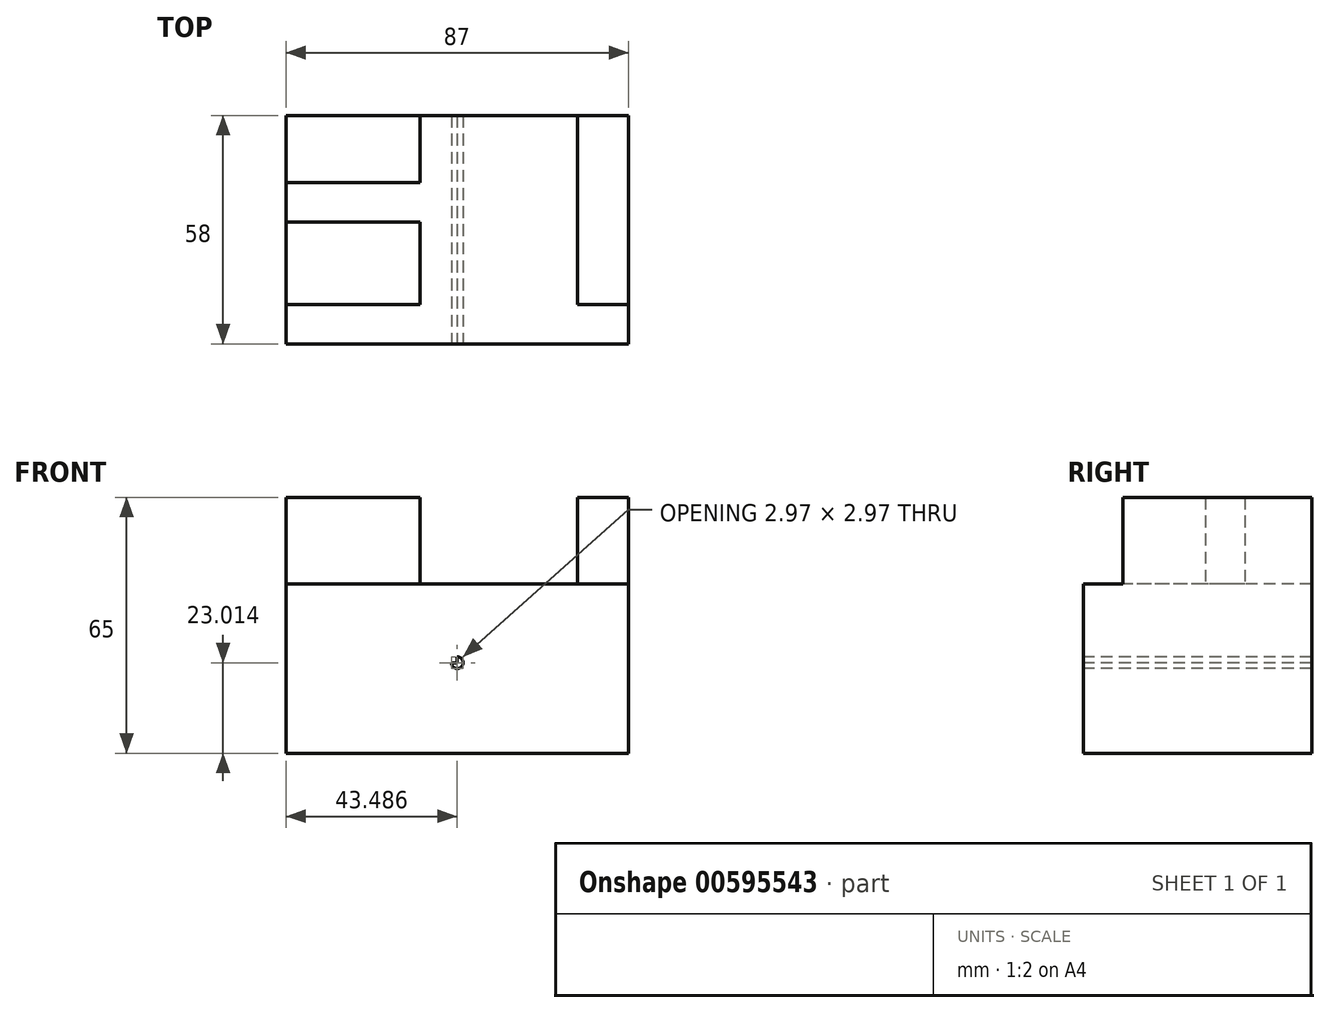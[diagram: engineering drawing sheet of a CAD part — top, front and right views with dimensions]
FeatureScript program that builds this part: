
annotation { "Feature Type Name" : "Feature", "Feature Type Description" : "" }
export const myFeature = defineFeature(function(context is Context, id is Id, definition is map)
    precondition{}
    {
        {
            var Q0;
            Q0=qCreatedBy(makeId("Top.planeOp"),FACE);
            var sketch = newSketch(context, id + "F0", { "sketchPlane" : qUnion([Q0])});
            skLineSegment(sketch, "E0.bottom", {"start": v(43.5, -29) * mm, "end": v(-43.5, -29) * mm});
            skLineSegment(sketch, "E0.top", {"start": v(43.5, 29) * mm, "end": v(-43.5, 29) * mm});
            skLineSegment(sketch, "E0.left", {"start": v(43.5, -29) * mm, "end": v(43.5, 29) * mm});
            skLineSegment(sketch, "E0.right", {"start": v(-43.5, -29) * mm, "end": v(-43.5, 29) * mm});
            skPoint(sketch, "E0.middle", {"position": v(0, 0) * mm});
            skSolve(sketch);
        }
        {
            var Q0;
            Q0=makeQuery(id+"F0.imprint","IMPRINT",FACE,{"disambiguationData":[TD([[makeQuery(id+"F0.imprint","IMPRINT",EDGE,{"derivedFrom":sQuery(id+"F0.wireOp",EDGE,"E0.bottom")}),-1.0]])]});
            extrude(context, id + "F1", {"entities" : qUnion([Q0]), "depth" : 65 * mm, "offsetDistance" : 25 * mm});
        }
        {
            var Q0;
            Q0=makeQuery(id+"F1.opExtrude","SWEPT_FACE",FACE,{"disambiguationData":[OSD([sQuery(id+"F0.wireOp",EDGE,"E0.right")])]});
            var sketch = newSketch(context, id + "F2", { "sketchPlane" : qUnion([Q0])});
            skLineSegment(sketch, "E1", {"start": v(-12, 65) * mm, "end": v(-12, 0) * mm});
            skLineSegment(sketch, "E2", {"start": v(-29, 43) * mm, "end": v(29, 43) * mm});
            skLineSegment(sketch, "E3", {"start": v(-2, 65) * mm, "end": v(-2, 0) * mm});
            skLineSegment(sketch, "E4", {"start": v(19, 65) * mm, "end": v(19, 0) * mm});
            skSolve(sketch);
        }
        {
            var Q0;
            {var subQ0=sQuery(id+"F2.wireOp",EDGE,"E1");var subQ1=makeQuery(id+"F1.opExtrude","CAP_EDGE",EDGE,{"disambiguationData":[OSD([sQuery(id+"F0.wireOp",EDGE,"E0.right")])],"isStart":false});var subQ2=makeQuery(id+"F2.imprint","INTERSECT",VERTEX,{"derivedFrom":[subQ1,subQ0]});Q0=makeQuery(id+"F2.imprint","IMPRINT",FACE,{"disambiguationData":[TD([[makeQuery(id+"F2.imprint","IMPRINT",EDGE,{"disambiguationData":[TD([[subQ2,-1.0]])],"derivedFrom":subQ0}),1.0]])]});}
            extrude(context, id + "F3", {"entities" : qUnion([Q0]), "operationType" : NewBodyOperationType.REMOVE, "oppositeDirection" : true, "depth" : 74 * mm, "offsetDistance" : 25 * mm});
        }
        {
            var Q0;
            Q0=makeQuery(id+"F1.opExtrude","SWEPT_FACE",FACE,{"disambiguationData":[OSD([sQuery(id+"F0.wireOp",EDGE,"E0.bottom")])]});
            var sketch = newSketch(context, id + "F4", { "sketchPlane" : qUnion([Q0])});
            skLineSegment(sketch, "E5", {"start": v(-9.5, 65) * mm, "end": v(-9.5, 0) * mm});
            skLineSegment(sketch, "E6", {"start": v(30.5, 65) * mm, "end": v(30.5, 0) * mm});
            skLineSegment(sketch, "E7", {"start": v(-43.5, 43) * mm, "end": v(43.5, 43) * mm});
            skLineSegment(sketch, "E8", {"start": v(0, 65) * mm, "end": v(0, 0) * mm});
            skLineSegment(sketch, "E9", {"start": v(-43.5, 23) * mm, "end": v(43.5, 23) * mm});
            skCircle(sketch, "E10", {"center": v(0, 23) * mm, "radius": 1.5 * mm});
            skLineSegment(sketch, "E11", {"start": v(0, 23) * mm, "end": v(1.25, 22.18) * mm});
            skSolve(sketch);
        }
        {
            var Q0;
            {var subQ0=sQuery(id+"F4.wireOp",EDGE,"E5");var subQ1=makeQuery(id+"F1.opExtrude","CAP_EDGE",EDGE,{"disambiguationData":[OSD([sQuery(id+"F0.wireOp",EDGE,"E0.bottom")])],"isStart":false});var subQ2=makeQuery(id+"F4.imprint","INTERSECT",VERTEX,{"derivedFrom":[subQ1,subQ0]});Q0=makeQuery(id+"F4.imprint","IMPRINT",FACE,{"disambiguationData":[TD([[makeQuery(id+"F4.imprint","IMPRINT",EDGE,{"disambiguationData":[TD([[subQ2,-1.0]])],"derivedFrom":subQ0}),1.0]])]});}
            var Q1;
            {var subQ0=sQuery(id+"F4.wireOp",EDGE,"E6");var subQ1=makeQuery(id+"F1.opExtrude","CAP_EDGE",EDGE,{"disambiguationData":[OSD([sQuery(id+"F0.wireOp",EDGE,"E0.bottom")])],"isStart":false});var subQ2=makeQuery(id+"F4.imprint","INTERSECT",VERTEX,{"derivedFrom":[subQ1,subQ0]});Q1=makeQuery(id+"F4.imprint","IMPRINT",FACE,{"disambiguationData":[TD([[makeQuery(id+"F4.imprint","IMPRINT",EDGE,{"disambiguationData":[TD([[subQ2,-1.0]])],"derivedFrom":subQ0}),-1.0]])]});}
            extrude(context, id + "F5", {"entities" : qUnion([Q0, Q1]), "operationType" : NewBodyOperationType.REMOVE, "oppositeDirection" : true, "depth" : 58 * mm, "offsetDistance" : 25 * mm});
        }
        {
            var Q0;
            {var subQ1=sQuery(id+"F0.wireOp",EDGE,"E0.right");var subQ4=sQuery(id+"F2.wireOp",EDGE,"E4");var subQ6=makeQuery(id+"F1.opExtrude","CAP_EDGE",EDGE,{"disambiguationData":[OSD([subQ1])],"isStart":false});var subQ7=makeQuery(id+"F2.imprint","INTERSECT",VERTEX,{"derivedFrom":[subQ6,subQ4]});Q0=makeQuery(id+"F2.imprint","IMPRINT",FACE,{"disambiguationData":[TD([[makeQuery(id+"F2.imprint","IMPRINT",EDGE,{"disambiguationData":[TD([[subQ7,-1.0]])],"derivedFrom":subQ4}),1.0]])]});}
            extrude(context, id + "F6", {"entities" : qUnion([Q0]), "operationType" : NewBodyOperationType.REMOVE, "oppositeDirection" : true, "depth" : 90 * mm, "offsetDistance" : 25 * mm});
        }
        {
            var Q0;
            {var subQ1=sQuery(id+"F4.wireOp",EDGE,"E8");var subQ3=sQuery(id+"F4.wireOp",EDGE,"E10");var subQ4=makeQuery(id+"F4.imprint","INTERSECT",VERTEX,{"disambiguationData":[OD(0.0)],"derivedFrom":[subQ1,subQ3]});Q0=makeQuery(id+"F4.imprint","IMPRINT",FACE,{"disambiguationData":[TD([[makeQuery(id+"F4.imprint","IMPRINT",EDGE,{"disambiguationData":[TD([[subQ4,1.0]])],"derivedFrom":subQ3}),1.0]])]});}
            var Q1;
            {var subQ1=sQuery(id+"F4.wireOp",EDGE,"E8");var subQ3=sQuery(id+"F4.wireOp",EDGE,"E10");var subQ4=makeQuery(id+"F4.imprint","INTERSECT",VERTEX,{"disambiguationData":[OD(0.0)],"derivedFrom":[subQ1,subQ3]});Q1=makeQuery(id+"F4.imprint","IMPRINT",FACE,{"disambiguationData":[TD([[makeQuery(id+"F4.imprint","IMPRINT",EDGE,{"disambiguationData":[TD([[subQ4,-1.0]])],"derivedFrom":subQ3}),1.0]])]});}
            var Q2;
            {var subQ1=sQuery(id+"F4.wireOp",EDGE,"E8");var subQ3=sQuery(id+"F4.wireOp",EDGE,"E10");var subQ4=makeQuery(id+"F4.imprint","INTERSECT",VERTEX,{"disambiguationData":[OD(1.0)],"derivedFrom":[subQ1,subQ3]});Q2=makeQuery(id+"F4.imprint","IMPRINT",FACE,{"disambiguationData":[TD([[makeQuery(id+"F4.imprint","IMPRINT",EDGE,{"disambiguationData":[TD([[subQ4,1.0]])],"derivedFrom":subQ3}),1.0]])]});}
            var Q3;
            {var subQ0=sQuery(id+"F4.wireOp",EDGE,"E11");Q3=makeQuery(id+"F4.imprint","IMPRINT",FACE,{"disambiguationData":[TD([[makeQuery(id+"F4.imprint","IMPRINT",EDGE,{"derivedFrom":subQ0}),-1.0]])]});}
            var Q4;
            {var subQ0=sQuery(id+"F4.wireOp",EDGE,"E11");Q4=makeQuery(id+"F4.imprint","IMPRINT",FACE,{"disambiguationData":[TD([[makeQuery(id+"F4.imprint","IMPRINT",EDGE,{"derivedFrom":subQ0}),1.0]])]});}
            extrude(context, id + "F7", {"entities" : qUnion([Q0, Q1, Q2, Q3, Q4]), "operationType" : NewBodyOperationType.REMOVE, "oppositeDirection" : true, "depth" : 99 * mm, "offsetDistance" : 25 * mm});
        }
    });
